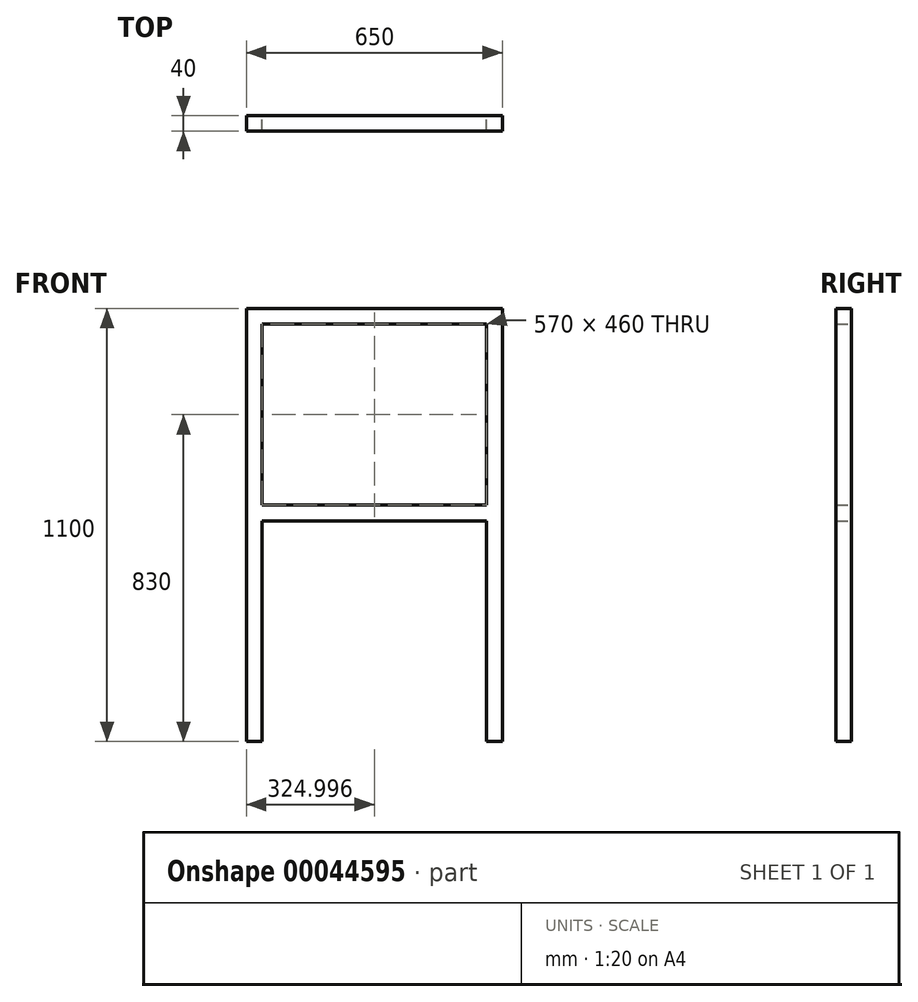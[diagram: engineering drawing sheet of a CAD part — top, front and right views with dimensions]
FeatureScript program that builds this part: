
annotation { "Feature Type Name" : "Feature", "Feature Type Description" : "" }
export const myFeature = defineFeature(function(context is Context, id is Id, definition is map)
    precondition{}
    {
        {
            var Q0;
            Q0=qCreatedBy(makeId("Front.planeOp"),FACE);
            var sketch = newSketch(context, id + "F0", { "sketchPlane" : qUnion([Q0])});
            skLineSegment(sketch, "E0.bottom", {"start": v(-956.36, -1100) * mm, "end": v(-916.36, -1100) * mm});
            skLineSegment(sketch, "E0.left", {"start": v(-956.36, -1100) * mm, "end": v(-956.36, 0) * mm});
            skLineSegment(sketch, "E0.right", {"start": v(-916.36, -1100) * mm, "end": v(-916.36, -40) * mm});
            skLineSegment(sketch, "E1.top", {"start": v(-916.36, -40) * mm, "end": v(-346.36, -40) * mm});
            skLineSegment(sketch, "E2.top", {"start": v(-346.36, -1100) * mm, "end": v(-306.36, -1100) * mm});
            skLineSegment(sketch, "E2.left", {"start": v(-346.36, -40) * mm, "end": v(-346.36, -1100) * mm});
            skLineSegment(sketch, "E2.right", {"start": v(-306.36, 0) * mm, "end": v(-306.36, -1100) * mm});
            skLineSegment(sketch, "E3", {"start": v(-956.36, 0) * mm, "end": v(-306.36, 0) * mm});
            skLineSegment(sketch, "E4", {"start": v(-916.36, -500) * mm, "end": v(-346.36, -500) * mm});
            skLineSegment(sketch, "E5", {"start": v(-916.36, -540) * mm, "end": v(-346.36, -540) * mm});
            skSolve(sketch);
        }
        {
            var Q0;
            Q0=makeQuery(id+"F0.imprint","IMPRINT",FACE,{"disambiguationData":[TD([[makeQuery(id+"F0.imprint","IMPRINT",EDGE,{"derivedFrom":sQuery(id+"F0.wireOp",EDGE,"E0.bottom")}),1.0]])]});
            var Q1;
            {var subQ1=sQuery(id+"F0.wireOp",EDGE,"E4");Q1=makeQuery(id+"F0.imprint","IMPRINT",FACE,{"disambiguationData":[TD([[makeQuery(id+"F0.imprint","IMPRINT",EDGE,{"derivedFrom":subQ1}),-1.0]])]});}
            extrude(context, id + "F1", {"entities" : qUnion([Q0, Q1]), "depth" : 40 * mm});
        }
    });
